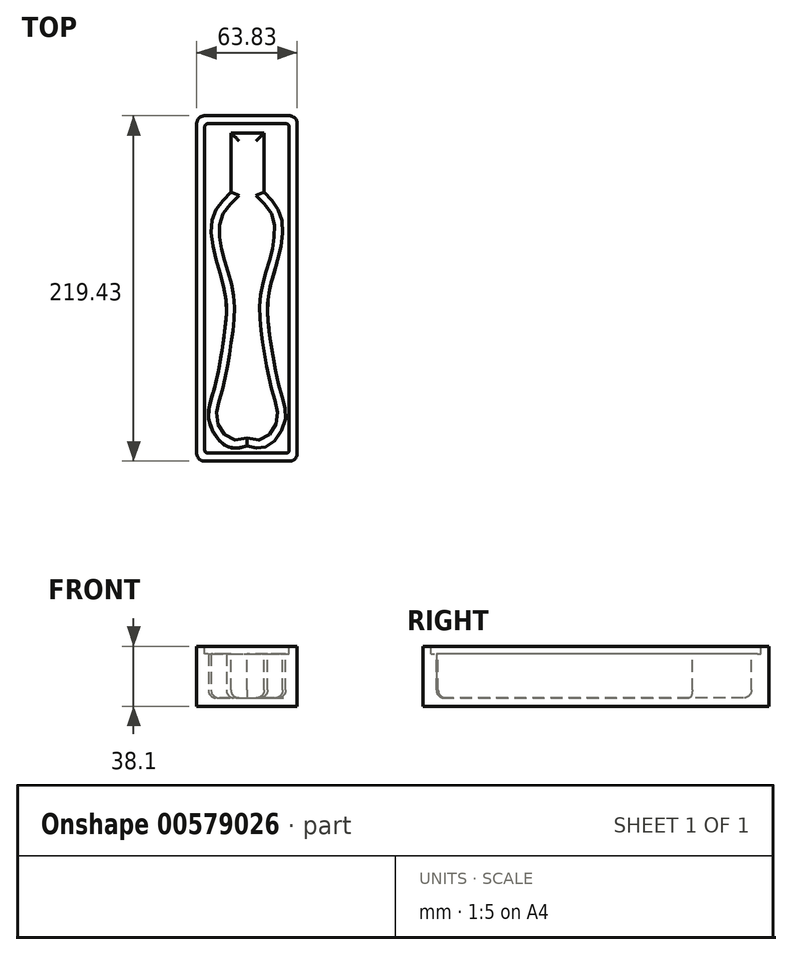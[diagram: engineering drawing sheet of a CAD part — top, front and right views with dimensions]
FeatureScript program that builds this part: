
annotation { "Feature Type Name" : "Feature", "Feature Type Description" : "" }
export const myFeature = defineFeature(function(context is Context, id is Id, definition is map)
    precondition{}
    {
        {
            var Q0;
            Q0=qCreatedBy(makeId("Top.planeOp"),FACE);
            var sketch = newSketch(context, id + "F0", { "sketchPlane" : qUnion([Q0])});
            skLineSegment(sketch, "E0.bottom", {"start": v(-42.79, 151.86) * mm, "end": v(21.04, 151.86) * mm});
            skLineSegment(sketch, "E0.top", {"start": v(-42.79, -67.57) * mm, "end": v(21.04, -67.57) * mm});
            skLineSegment(sketch, "E0.left", {"start": v(-42.79, 151.86) * mm, "end": v(-42.79, -67.57) * mm});
            skLineSegment(sketch, "E0.right", {"start": v(21.04, 151.86) * mm, "end": v(21.04, -67.57) * mm});
            skSolve(sketch);
        }
        {
            var Q0;
            Q0=makeQuery(id+"F0.imprint","IMPRINT",FACE,{"disambiguationData":[TD([[makeQuery(id+"F0.imprint","IMPRINT",EDGE,{"derivedFrom":sQuery(id+"F0.wireOp",EDGE,"E0.bottom")}),-1.0]])]});
            extrude(context, id + "F1", {"entities" : qUnion([Q0]), "depth" : 38.1 * mm, "offsetDistance" : 25.4 * mm});
        }
        {
            var Q0;
            Q0=makeQuery(id+"F1.opExtrude","SWEPT_EDGE",EDGE,{"disambiguationData":[OSD([sQuery(id+"F0.wireOp",EDGE,"E0.bottom"),sQuery(id+"F0.wireOp",EDGE,"E0.right")])]});
            var Q1;
            Q1=makeQuery(id+"F1.opExtrude","SWEPT_EDGE",EDGE,{"disambiguationData":[OSD([sQuery(id+"F0.wireOp",EDGE,"E0.top"),sQuery(id+"F0.wireOp",EDGE,"E0.right")])]});
            var Q2;
            Q2=makeQuery(id+"F1.opExtrude","SWEPT_EDGE",EDGE,{"disambiguationData":[OSD([sQuery(id+"F0.wireOp",EDGE,"E0.top"),sQuery(id+"F0.wireOp",EDGE,"E0.left")])]});
            var Q3;
            Q3=makeQuery(id+"F1.opExtrude","SWEPT_EDGE",EDGE,{"disambiguationData":[OSD([sQuery(id+"F0.wireOp",EDGE,"E0.bottom"),sQuery(id+"F0.wireOp",EDGE,"E0.left")])]});
            fillet(context, id + "F2", {"entities" : qUnion([Q0, Q1, Q2, Q3]), "radius" : 5.08 * mm, "tangentPropagation" : true, "allowEdgeOverflow" : false});
        }
        {
            var Q0;
            Q0=makeQuery(id+"F1.opExtrude","CAP_FACE",FACE,{"disambiguationData":[OSD([sQuery(id+"F0.wireOp",EDGE,"E0.bottom"),sQuery(id+"F0.wireOp",EDGE,"E0.top"),sQuery(id+"F0.wireOp",EDGE,"E0.left"),sQuery(id+"F0.wireOp",EDGE,"E0.right")])],"isStart":false});
            var sketch = newSketch(context, id + "F3", { "sketchPlane" : qUnion([Q0])});
            skLineSegment(sketch, "E1.bottom", {"start": v(-37.7, 146.78) * mm, "end": v(15.96, 146.78) * mm});
            skLineSegment(sketch, "E1.top", {"start": v(-37.7, -62.49) * mm, "end": v(15.96, -62.49) * mm});
            skLineSegment(sketch, "E1.left", {"start": v(-37.7, 146.78) * mm, "end": v(-37.7, -62.49) * mm});
            skLineSegment(sketch, "E1.right", {"start": v(15.96, 146.78) * mm, "end": v(15.96, -62.49) * mm});
            skSolve(sketch);
        }
        {
            var Q0;
            Q0=makeQuery(id+"F3.imprint","IMPRINT",FACE,{"disambiguationData":[TD([[makeQuery(id+"F3.imprint","IMPRINT",EDGE,{"derivedFrom":sQuery(id+"F3.wireOp",EDGE,"E1.bottom")}),-1.0]])]});
            extrude(context, id + "F4", {"entities" : qUnion([Q0]), "operationType" : NewBodyOperationType.REMOVE, "oppositeDirection" : true, "depth" : 5 * mm, "offsetDistance" : 25.4 * mm});
        }
        {
            var Q0;
            Q0=makeQuery(id+"F4.boolean.opBoolean","COPY",EDGE,{"derivedFrom":makeQuery(id+"F4.opExtrude","SWEPT_EDGE",EDGE,{"disambiguationData":[OSD([sQuery(id+"F3.wireOp",EDGE,"E1.bottom"),sQuery(id+"F3.wireOp",EDGE,"E1.left")])]})});
            var Q1;
            Q1=makeQuery(id+"F4.boolean.opBoolean","COPY",EDGE,{"derivedFrom":makeQuery(id+"F4.opExtrude","SWEPT_EDGE",EDGE,{"disambiguationData":[OSD([sQuery(id+"F3.wireOp",EDGE,"E1.bottom"),sQuery(id+"F3.wireOp",EDGE,"E1.right")])]})});
            var Q2;
            Q2=makeQuery(id+"F4.boolean.opBoolean","COPY",EDGE,{"derivedFrom":makeQuery(id+"F4.opExtrude","SWEPT_EDGE",EDGE,{"disambiguationData":[OSD([sQuery(id+"F3.wireOp",EDGE,"E1.top"),sQuery(id+"F3.wireOp",EDGE,"E1.left")])]})});
            var Q3;
            Q3=makeQuery(id+"F4.boolean.opBoolean","COPY",EDGE,{"derivedFrom":makeQuery(id+"F4.opExtrude","SWEPT_EDGE",EDGE,{"disambiguationData":[OSD([sQuery(id+"F3.wireOp",EDGE,"E1.top"),sQuery(id+"F3.wireOp",EDGE,"E1.right")])]})});
            fillet(context, id + "F5", {"entities" : qUnion([Q0, Q1, Q2, Q3]), "radius" : 2 * mm, "tangentPropagation" : true, "allowEdgeOverflow" : false});
        }
        {
            var Q0;
            Q0=makeQuery(id+"F4.boolean.opBoolean","COPY",FACE,{"derivedFrom":makeQuery(id+"F4.opExtrude","CAP_FACE",FACE,{"disambiguationData":[OSD([sQuery(id+"F3.wireOp",EDGE,"E1.bottom"),sQuery(id+"F3.wireOp",EDGE,"E1.top"),sQuery(id+"F3.wireOp",EDGE,"E1.left"),sQuery(id+"F3.wireOp",EDGE,"E1.right")])],"isStart":false})});
            var sketch = newSketch(context, id + "F6", { "sketchPlane" : qUnion([Q0])});
            skLineSegment(sketch, "E2", {"start": v(-10.87, 140.9) * mm, "end": v(0, 140.9) * mm});
            skPoint(sketch, "E2.startSnap0", {"position": v(-10.87, 146.78) * mm});
            skLineSegment(sketch, "E3", {"start": v(-10.87, 140.9) * mm, "end": v(-21.03, 140.9) * mm});
            skLineSegment(sketch, "E4", {"start": v(-21.03, 140.9) * mm, "end": v(-21.03, 103.33) * mm});
            skLineSegment(sketch, "E5", {"start": v(0, 140.9) * mm, "end": v(0, 103.33) * mm});
            skPoint(sketch, "E6.8.internal.snap0", {"position": v(-10.87, -62.49) * mm});
            skFitSpline(sketch, "E6", {"points": [v(0, 103.33) * mm, v(10.6, 88.32) * mm, v(9.5, 63.47) * mm, v(2.6, 36.12) * mm, v(4.26, 7.95) * mm, v(10.06, -22.15) * mm, v(13.37, -41.76) * mm, v(2.05, -58.05) * mm, v(-10.87, -58.05) * mm], "startDerivative": vector(115.7, -119.28) * mm, "endDerivative": vector(-138.25, 32.28) * mm});
            skFitSpline(sketch, "E7.MirrorCS", {"points": [v(-21.03, 103.33) * mm, v(-32.36, 88.32) * mm, v(-31.25, 63.47) * mm, v(-24.35, 36.12) * mm, v(-26, 7.95) * mm, v(-31.8, -22.15) * mm, v(-35.12, -41.76) * mm, v(-23.8, -58.05) * mm, v(-10.87, -58.05) * mm], "startDerivative": vector(-115.7, -119.28) * mm, "endDerivative": vector(138.25, 32.28) * mm});
            skSolve(sketch);
        }
        {
            var Q0;
            Q0=makeQuery(id+"F6.imprint","IMPRINT",FACE,{"disambiguationData":[TD([[makeQuery(id+"F6.imprint","IMPRINT",EDGE,{"derivedFrom":sQuery(id+"F6.wireOp",EDGE,"E2")}),-1.0]])]});
            extrude(context, id + "F7", {"entities" : qUnion([Q0]), "operationType" : NewBodyOperationType.REMOVE, "oppositeDirection" : true, "depth" : 27.94 * mm, "offsetDistance" : 25.4 * mm});
        }
        {
            var Q0;
            Q0=makeQuery(id+"F7.boolean.opBoolean","COPY",EDGE,{"derivedFrom":makeQuery(id+"F7.opExtrude","CAP_EDGE",EDGE,{"disambiguationData":[OSD([sQuery(id+"F6.wireOp",EDGE,"E6")])],"isStart":false})});
            var Q1;
            Q1=makeQuery(id+"F7.boolean.opBoolean","COPY",EDGE,{"derivedFrom":makeQuery(id+"F7.opExtrude","CAP_EDGE",EDGE,{"disambiguationData":[OSD([sQuery(id+"F6.wireOp",EDGE,"E5")])],"isStart":false})});
            var Q2;
            Q2=makeQuery(id+"F7.boolean.opBoolean","COPY",EDGE,{"derivedFrom":makeQuery(id+"F7.opExtrude","CAP_EDGE",EDGE,{"disambiguationData":[OSD([sQuery(id+"F6.wireOp",EDGE,"E2"),sQuery(id+"F6.wireOp",EDGE,"E3")])],"isStart":false})});
            var Q3;
            Q3=makeQuery(id+"F7.boolean.opBoolean","COPY",EDGE,{"derivedFrom":makeQuery(id+"F7.opExtrude","CAP_EDGE",EDGE,{"disambiguationData":[OSD([sQuery(id+"F6.wireOp",EDGE,"E4")])],"isStart":false})});
            var Q4;
            Q4=makeQuery(id+"F7.boolean.opBoolean","COPY",FACE,{"derivedFrom":makeQuery(id+"F7.opExtrude","CAP_FACE",FACE,{"disambiguationData":[OSD([sQuery(id+"F6.wireOp",EDGE,"E2"),sQuery(id+"F6.wireOp",EDGE,"E3"),sQuery(id+"F6.wireOp",EDGE,"E4"),sQuery(id+"F6.wireOp",EDGE,"E5"),sQuery(id+"F6.wireOp",EDGE,"E6"),sQuery(id+"F6.wireOp",EDGE,"E7.MirrorCS")])],"isStart":false})});
            fillet(context, id + "F8", {"entities" : qUnion([Q0, Q1, Q2, Q3, Q4]), "radius" : 5.08 * mm, "tangentPropagation" : true, "allowEdgeOverflow" : false});
        }
    });
